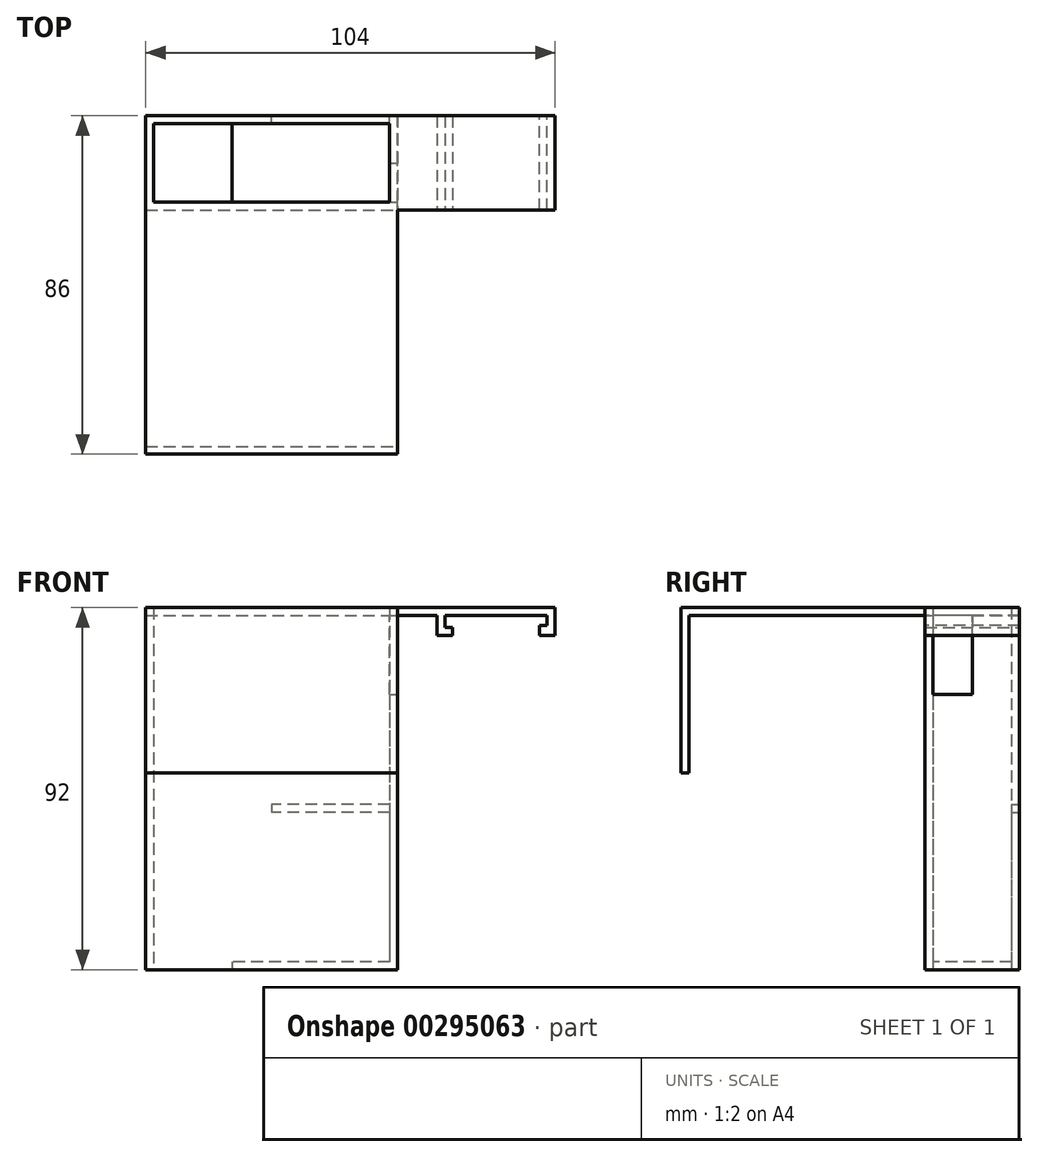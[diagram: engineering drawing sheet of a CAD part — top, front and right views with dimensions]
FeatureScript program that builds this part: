
annotation { "Feature Type Name" : "Feature", "Feature Type Description" : "" }
export const myFeature = defineFeature(function(context is Context, id is Id, definition is map)
    precondition{}
    {
        {
            var Q0;
            Q0=qCreatedBy(makeId("Top.planeOp"),FACE);
            var sketch = newSketch(context, id + "F0", { "sketchPlane" : qUnion([Q0])});
            skLineSegment(sketch, "E0.bottom", {"start": v(32, 32) * mm, "end": v(-32, 32) * mm});
            skLineSegment(sketch, "E0.top", {"start": v(32, -32) * mm, "end": v(-32, -32) * mm});
            skLineSegment(sketch, "E0.left", {"start": v(32, 32) * mm, "end": v(32, -32) * mm});
            skLineSegment(sketch, "E0.right", {"start": v(-32, 32) * mm, "end": v(-32, -32) * mm});
            skPoint(sketch, "E0.middle", {"position": v(0, 0) * mm});
            skSolve(sketch);
        }
        {
            var Q0;
            Q0=makeQuery(id+"F0.imprint","IMPRINT",FACE,{"disambiguationData":[TD([[makeQuery(id+"F0.imprint","IMPRINT",EDGE,{"derivedFrom":sQuery(id+"F0.wireOp",EDGE,"E0.bottom")}),1.0]])]});
            extrude(context, id + "F1", {"entities" : qUnion([Q0]), "depth" : 2 * mm});
        }
        {
            var Q0;
            Q0=makeQuery(id+"F1.opExtrude","CAP_FACE",FACE,{"disambiguationData":[OSD([sQuery(id+"F0.wireOp",EDGE,"E0.bottom"),sQuery(id+"F0.wireOp",EDGE,"E0.top"),sQuery(id+"F0.wireOp",EDGE,"E0.left"),sQuery(id+"F0.wireOp",EDGE,"E0.right")])],"isStart":true});
            var sketch = newSketch(context, id + "F2", { "sketchPlane" : qUnion([Q0])});
            skLineSegment(sketch, "E1.bottom", {"start": v(-32, 32) * mm, "end": v(32, 32) * mm});
            skLineSegment(sketch, "E1.top", {"start": v(-32, 30) * mm, "end": v(32, 30) * mm});
            skLineSegment(sketch, "E1.left", {"start": v(-32, 32) * mm, "end": v(-32, 30) * mm});
            skLineSegment(sketch, "E1.right", {"start": v(32, 32) * mm, "end": v(32, 30) * mm});
            skLineSegment(sketch, "E2.bottom", {"start": v(-32, -32) * mm, "end": v(32, -32) * mm});
            skLineSegment(sketch, "E2.top", {"start": v(-32, -30) * mm, "end": v(32, -30) * mm});
            skLineSegment(sketch, "E2.left", {"start": v(-32, -32) * mm, "end": v(-32, -30) * mm});
            skLineSegment(sketch, "E2.right", {"start": v(32, -32) * mm, "end": v(32, -30) * mm});
            skSolve(sketch);
        }
        {
            var Q0;
            Q0=makeQuery(id+"F2.imprint","IMPRINT",FACE,{"disambiguationData":[TD([[makeQuery(id+"F2.imprint","IMPRINT",EDGE,{"derivedFrom":sQuery(id+"F2.wireOp",EDGE,"E1.bottom")}),1.0]])]});
            extrude(context, id + "F3", {"entities" : qUnion([Q0]), "operationType" : NewBodyOperationType.ADD, "depth" : 25 * mm});
        }
        {
            var Q0;
            Q0=makeQuery(id+"F1.opExtrude","CAP_FACE",FACE,{"disambiguationData":[OSD([sQuery(id+"F0.wireOp",EDGE,"E0.bottom"),sQuery(id+"F0.wireOp",EDGE,"E0.top"),sQuery(id+"F0.wireOp",EDGE,"E0.left"),sQuery(id+"F0.wireOp",EDGE,"E0.right")])],"isStart":true});
            var sketch = newSketch(context, id + "F4", { "sketchPlane" : qUnion([Q0])});
            skLineSegment(sketch, "E3.bottom", {"start": v(-32, -32) * mm, "end": v(32, -32) * mm});
            skLineSegment(sketch, "E3.top", {"start": v(-32, -30) * mm, "end": v(32, -30) * mm});
            skLineSegment(sketch, "E3.left", {"start": v(-32, -32) * mm, "end": v(-32, -30) * mm});
            skLineSegment(sketch, "E3.right", {"start": v(32, -32) * mm, "end": v(32, -30) * mm});
            skSolve(sketch);
        }
        {
            var Q0;
            Q0=makeQuery(id+"F4.imprint","IMPRINT",FACE,{"disambiguationData":[TD([[makeQuery(id+"F4.imprint","IMPRINT",EDGE,{"derivedFrom":sQuery(id+"F4.wireOp",EDGE,"E3.bottom")}),-1.0]])]});
            extrude(context, id + "F5", {"entities" : qUnion([Q0]), "operationType" : NewBodyOperationType.ADD, "depth" : 90 * mm});
        }
        {
            var Q0;
            Q0=makeQuery(id+"F5.boolean.opBoolean","MERGE",FACE,{"derivedFrom":[makeQuery(id+"F1.opExtrude","SWEPT_FACE",FACE,{"disambiguationData":[OSD([sQuery(id+"F0.wireOp",EDGE,"E0.bottom")])]}),makeQuery(id+"F5.opExtrude","SWEPT_FACE",FACE,{"disambiguationData":[OSD([sQuery(id+"F4.wireOp",EDGE,"E3.bottom")])]})]});
            var sketch = newSketch(context, id + "F6", { "sketchPlane" : qUnion([Q0])});
            skLineSegment(sketch, "E4.bottom", {"start": v(-32, 2) * mm, "end": v(-30, 2) * mm});
            skLineSegment(sketch, "E4.top", {"start": v(-32, -90) * mm, "end": v(-30, -90) * mm});
            skLineSegment(sketch, "E4.left", {"start": v(-32, 2) * mm, "end": v(-32, -90) * mm});
            skLineSegment(sketch, "E4.right", {"start": v(-30, 2) * mm, "end": v(-30, -90) * mm});
            skSolve(sketch);
        }
        {
            var Q0;
            Q0=makeQuery(id+"F6.imprint","IMPRINT",FACE,{"disambiguationData":[TD([[makeQuery(id+"F6.imprint","IMPRINT",EDGE,{"derivedFrom":sQuery(id+"F6.wireOp",EDGE,"E4.bottom")}),-1.0]])]});
            extrude(context, id + "F7", {"entities" : qUnion([Q0]), "operationType" : NewBodyOperationType.ADD, "depth" : 22 * mm});
        }
        {
            var Q0;
            Q0=makeQuery(id+"F5.boolean.opBoolean","MERGE",FACE,{"derivedFrom":[makeQuery(id+"F1.opExtrude","SWEPT_FACE",FACE,{"disambiguationData":[OSD([sQuery(id+"F0.wireOp",EDGE,"E0.bottom")])]}),makeQuery(id+"F5.opExtrude","SWEPT_FACE",FACE,{"disambiguationData":[OSD([sQuery(id+"F4.wireOp",EDGE,"E3.bottom")])]})]});
            var sketch = newSketch(context, id + "F8", { "sketchPlane" : qUnion([Q0])});
            skLineSegment(sketch, "E5.bottom", {"start": v(32, 2) * mm, "end": v(30, 2) * mm});
            skLineSegment(sketch, "E5.top", {"start": v(32, -90) * mm, "end": v(30, -90) * mm});
            skLineSegment(sketch, "E5.left", {"start": v(32, 2) * mm, "end": v(32, -90) * mm});
            skLineSegment(sketch, "E5.right", {"start": v(30, 2) * mm, "end": v(30, -90) * mm});
            skSolve(sketch);
        }
        {
            var Q0;
            Q0=makeQuery(id+"F8.imprint","IMPRINT",FACE,{"disambiguationData":[TD([[makeQuery(id+"F8.imprint","IMPRINT",EDGE,{"derivedFrom":sQuery(id+"F8.wireOp",EDGE,"E5.bottom")}),-1.0]])]});
            extrude(context, id + "F9", {"entities" : qUnion([Q0]), "operationType" : NewBodyOperationType.ADD, "depth" : 22 * mm});
        }
        {
            var Q0;
            Q0=makeQuery(id+"F7.opExtrude","SWEPT_FACE",FACE,{"disambiguationData":[OSD([sQuery(id+"F6.wireOp",EDGE,"E4.right")])]});
            var sketch = newSketch(context, id + "F10", { "sketchPlane" : qUnion([Q0])});
            skLineSegment(sketch, "E6.bottom", {"start": v(-54, 2) * mm, "end": v(-52, 2) * mm});
            skLineSegment(sketch, "E6.top", {"start": v(-54, -90) * mm, "end": v(-52, -90) * mm});
            skLineSegment(sketch, "E6.left", {"start": v(-54, 2) * mm, "end": v(-54, -90) * mm});
            skLineSegment(sketch, "E6.right", {"start": v(-52, 2) * mm, "end": v(-52, -90) * mm});
            skSolve(sketch);
        }
        {
            var Q0;
            Q0=makeQuery(id+"F10.imprint","IMPRINT",FACE,{"disambiguationData":[TD([[makeQuery(id+"F10.imprint","IMPRINT",EDGE,{"derivedFrom":sQuery(id+"F10.wireOp",EDGE,"E6.bottom")}),-1.0]])]});
            extrude(context, id + "F11", {"entities" : qUnion([Q0]), "operationType" : NewBodyOperationType.ADD, "depth" : 60 * mm});
        }
        {
            var Q0;
            Q0=makeQuery(id+"F5.boolean.opBoolean","MERGE",FACE,{"derivedFrom":[makeQuery(id+"F1.opExtrude","SWEPT_FACE",FACE,{"disambiguationData":[OSD([sQuery(id+"F0.wireOp",EDGE,"E0.bottom")])]}),makeQuery(id+"F5.opExtrude","SWEPT_FACE",FACE,{"disambiguationData":[OSD([sQuery(id+"F4.wireOp",EDGE,"E3.bottom")])]})]});
            var sketch = newSketch(context, id + "F12", { "sketchPlane" : qUnion([Q0])});
            skLineSegment(sketch, "E7.bottom", {"start": v(-30, -90) * mm, "end": v(30, -90) * mm});
            skLineSegment(sketch, "E7.top", {"start": v(-30, -88) * mm, "end": v(30, -88) * mm});
            skLineSegment(sketch, "E7.left", {"start": v(-30, -90) * mm, "end": v(-30, -88) * mm});
            skLineSegment(sketch, "E7.right", {"start": v(30, -90) * mm, "end": v(30, -88) * mm});
            skSolve(sketch);
        }
        {
            var Q0;
            Q0=makeQuery(id+"F12.imprint","IMPRINT",FACE,{"disambiguationData":[TD([[makeQuery(id+"F12.imprint","IMPRINT",EDGE,{"derivedFrom":sQuery(id+"F12.wireOp",EDGE,"E7.bottom")}),1.0]])]});
            extrude(context, id + "F13", {"entities" : qUnion([Q0]), "operationType" : NewBodyOperationType.ADD, "depth" : 20 * mm});
        }
        {
            var Q0;
            Q0=makeQuery(id+"F7.boolean.opBoolean","MERGE",FACE,{"derivedFrom":[makeQuery(id+"F5.boolean.opBoolean","MERGE",FACE,{"derivedFrom":[makeQuery(id+"F3.boolean.opBoolean","MERGE",FACE,{"derivedFrom":[makeQuery(id+"F1.opExtrude","SWEPT_FACE",FACE,{"disambiguationData":[OSD([sQuery(id+"F0.wireOp",EDGE,"E0.left")])]}),makeQuery(id+"F3.opExtrude","SWEPT_FACE",FACE,{"disambiguationData":[OSD([sQuery(id+"F2.wireOp",EDGE,"E1.right")])]})]}),makeQuery(id+"F5.opExtrude","SWEPT_FACE",FACE,{"disambiguationData":[OSD([sQuery(id+"F4.wireOp",EDGE,"E3.right")])]})]}),makeQuery(id+"F7.opExtrude","SWEPT_FACE",FACE,{"disambiguationData":[OSD([sQuery(id+"F6.wireOp",EDGE,"E4.left")])]})]});
            var sketch = newSketch(context, id + "F14", { "sketchPlane" : qUnion([Q0])});
            skLineSegment(sketch, "E8.bottom", {"start": v(32, 0) * mm, "end": v(42, 0) * mm});
            skLineSegment(sketch, "E8.top", {"start": v(32, -20) * mm, "end": v(42, -20) * mm});
            skLineSegment(sketch, "E8.left", {"start": v(32, 0) * mm, "end": v(32, -20) * mm});
            skLineSegment(sketch, "E8.right", {"start": v(42, 0) * mm, "end": v(42, -20) * mm});
            skSolve(sketch);
        }
        {
            var Q0;
            Q0=makeQuery(id+"F14.imprint","IMPRINT",FACE,{"disambiguationData":[TD([[makeQuery(id+"F14.imprint","IMPRINT",EDGE,{"derivedFrom":sQuery(id+"F14.wireOp",EDGE,"E8.bottom")}),-1.0]])]});
            extrude(context, id + "F15", {"entities" : qUnion([Q0]), "operationType" : NewBodyOperationType.REMOVE, "oppositeDirection" : true, "depth" : 25 * mm});
        }
        {
            var Q0;
            Q0=makeQuery(id+"F13.boolean.opBoolean","MERGE",FACE,{"derivedFrom":[makeQuery(id+"F11.boolean.opBoolean","MERGE",FACE,{"derivedFrom":[makeQuery(id+"F9.boolean.opBoolean","MERGE",FACE,{"derivedFrom":[makeQuery(id+"F7.boolean.opBoolean","MERGE",FACE,{"derivedFrom":[makeQuery(id+"F5.opExtrude","CAP_FACE",FACE,{"disambiguationData":[OSD([sQuery(id+"F4.wireOp",EDGE,"E3.bottom"),sQuery(id+"F4.wireOp",EDGE,"E3.top"),sQuery(id+"F4.wireOp",EDGE,"E3.left"),sQuery(id+"F4.wireOp",EDGE,"E3.right")])],"isStart":false}),makeQuery(id+"F7.opExtrude","SWEPT_FACE",FACE,{"disambiguationData":[OSD([sQuery(id+"F6.wireOp",EDGE,"E4.top")])]})]}),makeQuery(id+"F9.opExtrude","SWEPT_FACE",FACE,{"disambiguationData":[OSD([sQuery(id+"F8.wireOp",EDGE,"E5.top")])]})]}),makeQuery(id+"F11.opExtrude","SWEPT_FACE",FACE,{"disambiguationData":[OSD([sQuery(id+"F10.wireOp",EDGE,"E6.top")])]})]}),makeQuery(id+"F13.opExtrude","SWEPT_FACE",FACE,{"disambiguationData":[OSD([sQuery(id+"F12.wireOp",EDGE,"E7.bottom")])]})]});
            var sketch = newSketch(context, id + "F16", { "sketchPlane" : qUnion([Q0])});
            skLineSegment(sketch, "E9.bottom", {"start": v(-30, -32) * mm, "end": v(-10, -32) * mm});
            skLineSegment(sketch, "E9.top", {"start": v(-30, -52) * mm, "end": v(-10, -52) * mm});
            skLineSegment(sketch, "E9.left", {"start": v(-30, -32) * mm, "end": v(-30, -52) * mm});
            skLineSegment(sketch, "E9.right", {"start": v(-10, -32) * mm, "end": v(-10, -52) * mm});
            skSolve(sketch);
        }
        {
            var Q0;
            Q0=makeQuery(id+"F16.imprint","IMPRINT",FACE,{"disambiguationData":[TD([[makeQuery(id+"F16.imprint","IMPRINT",EDGE,{"derivedFrom":sQuery(id+"F16.wireOp",EDGE,"E9.bottom")}),-1.0]])]});
            extrude(context, id + "F17", {"entities" : qUnion([Q0]), "operationType" : NewBodyOperationType.REMOVE, "oppositeDirection" : true, "depth" : 25 * mm});
        }
        {
            var Q0;
            Q0=makeQuery(id+"F3.opExtrude","CAP_FACE",FACE,{"disambiguationData":[OSD([sQuery(id+"F2.wireOp",EDGE,"E1.bottom"),sQuery(id+"F2.wireOp",EDGE,"E1.top"),sQuery(id+"F2.wireOp",EDGE,"E1.left"),sQuery(id+"F2.wireOp",EDGE,"E1.right")])],"isStart":false});
            extrude(context, id + "F18", {"entities" : qUnion([Q0]), "operationType" : NewBodyOperationType.ADD, "depth" : 15 * mm});
        }
        {
            var Q0;
            Q0=makeQuery(id+"F11.boolean.opBoolean","MERGE",FACE,{"derivedFrom":[makeQuery(id+"F7.opExtrude","CAP_FACE",FACE,{"disambiguationData":[OSD([sQuery(id+"F6.wireOp",EDGE,"E4.bottom"),sQuery(id+"F6.wireOp",EDGE,"E4.top"),sQuery(id+"F6.wireOp",EDGE,"E4.left"),sQuery(id+"F6.wireOp",EDGE,"E4.right")])],"isStart":false}),makeQuery(id+"F9.opExtrude","CAP_FACE",FACE,{"disambiguationData":[OSD([sQuery(id+"F8.wireOp",EDGE,"E5.bottom"),sQuery(id+"F8.wireOp",EDGE,"E5.top"),sQuery(id+"F8.wireOp",EDGE,"E5.left"),sQuery(id+"F8.wireOp",EDGE,"E5.right")])],"isStart":false}),makeQuery(id+"F11.opExtrude","SWEPT_FACE",FACE,{"disambiguationData":[OSD([sQuery(id+"F10.wireOp",EDGE,"E6.left")])]})]});
            var sketch = newSketch(context, id + "F19", { "sketchPlane" : qUnion([Q0])});
            skLineSegment(sketch, "E10.bottom", {"start": v(-30, -48) * mm, "end": v(0, -48) * mm});
            skLineSegment(sketch, "E10.top", {"start": v(-30, -50) * mm, "end": v(0, -50) * mm});
            skLineSegment(sketch, "E10.left", {"start": v(-30, -48) * mm, "end": v(-30, -50) * mm});
            skLineSegment(sketch, "E10.right", {"start": v(0, -48) * mm, "end": v(0, -50) * mm});
            skSolve(sketch);
        }
        {
            var Q0;
            Q0=makeQuery(id+"F19.imprint","IMPRINT",FACE,{"disambiguationData":[TD([[makeQuery(id+"F19.imprint","IMPRINT",EDGE,{"derivedFrom":sQuery(id+"F19.wireOp",EDGE,"E10.bottom")}),-1.0]])]});
            extrude(context, id + "F20", {"entities" : qUnion([Q0]), "operationType" : NewBodyOperationType.REMOVE, "oppositeDirection" : true, "depth" : 2 * mm});
        }
        {
            var Q0;
            {var subQ0=sQuery(id+"F2.wireOp",EDGE,"E1.right");Q0=makeQuery(id+"F18.boolean.opBoolean","MERGE",FACE,{"derivedFrom":[makeQuery(id+"F7.boolean.opBoolean","MERGE",FACE,{"derivedFrom":[makeQuery(id+"F5.boolean.opBoolean","MERGE",FACE,{"derivedFrom":[makeQuery(id+"F3.boolean.opBoolean","MERGE",FACE,{"derivedFrom":[makeQuery(id+"F1.opExtrude","SWEPT_FACE",FACE,{"disambiguationData":[OSD([sQuery(id+"F0.wireOp",EDGE,"E0.left")])]}),makeQuery(id+"F3.opExtrude","SWEPT_FACE",FACE,{"disambiguationData":[OSD([subQ0])]})]}),makeQuery(id+"F5.opExtrude","SWEPT_FACE",FACE,{"disambiguationData":[OSD([sQuery(id+"F4.wireOp",EDGE,"E3.right")])]})]}),makeQuery(id+"F7.opExtrude","SWEPT_FACE",FACE,{"disambiguationData":[OSD([sQuery(id+"F6.wireOp",EDGE,"E4.left")])]})]}),makeQuery(id+"F18.opExtrude","SWEPT_FACE",FACE,{"disambiguationData":[OSD([subQ0])]})]});}
            var sketch = newSketch(context, id + "F21", { "sketchPlane" : qUnion([Q0])});
            skLineSegment(sketch, "E11.bottom", {"start": v(30, 0) * mm, "end": v(54, 0) * mm});
            skLineSegment(sketch, "E11.top", {"start": v(30, 2) * mm, "end": v(54, 2) * mm});
            skLineSegment(sketch, "E11.left", {"start": v(30, 0) * mm, "end": v(30, 2) * mm});
            skLineSegment(sketch, "E11.right", {"start": v(54, 0) * mm, "end": v(54, 2) * mm});
            skSolve(sketch);
        }
        {
            var Q0;
            Q0=makeQuery(id+"F21.imprint","IMPRINT",FACE,{"disambiguationData":[TD([[makeQuery(id+"F21.imprint","IMPRINT",EDGE,{"derivedFrom":sQuery(id+"F21.wireOp",EDGE,"E11.top")}),1.0]])]});
            extrude(context, id + "F22", {"entities" : qUnion([Q0]), "operationType" : NewBodyOperationType.ADD, "depth" : 40 * mm});
        }
        {
            var Q0;
            Q0=makeQuery(id+"F22.boolean.opBoolean","MERGE",FACE,{"derivedFrom":[makeQuery(id+"F15.boolean.opBoolean","COPY",FACE,{"derivedFrom":makeQuery(id+"F15.opExtrude","SWEPT_FACE",FACE,{"disambiguationData":[OSD([sQuery(id+"F14.wireOp",EDGE,"E8.bottom")])]})}),makeQuery(id+"F22.opExtrude","SWEPT_FACE",FACE,{"disambiguationData":[OSD([sQuery(id+"F21.wireOp",EDGE,"E11.bottom")])]})]});
            var sketch = newSketch(context, id + "F23", { "sketchPlane" : qUnion([Q0])});
            skLineSegment(sketch, "E12.bottom", {"start": v(72, -30) * mm, "end": v(70, -30) * mm});
            skLineSegment(sketch, "E12.top", {"start": v(72, -54) * mm, "end": v(70, -54) * mm});
            skLineSegment(sketch, "E12.left", {"start": v(72, -30) * mm, "end": v(72, -54) * mm});
            skLineSegment(sketch, "E12.right", {"start": v(70, -30) * mm, "end": v(70, -54) * mm});
            skLineSegment(sketch, "E13.right", {"start": v(44, -54) * mm, "end": v(44, -47.91) * mm});
            skLineSegment(sketch, "E14.bottom", {"start": v(44, -54) * mm, "end": v(42, -54) * mm});
            skLineSegment(sketch, "E14.top", {"start": v(44, -30) * mm, "end": v(42, -30) * mm});
            skLineSegment(sketch, "E14.left", {"start": v(44, -54) * mm, "end": v(44, -30) * mm});
            skLineSegment(sketch, "E14.right", {"start": v(42, -54) * mm, "end": v(42, -30) * mm});
            skSolve(sketch);
        }
        {
            var Q0;
            Q0=makeQuery(id+"F23.imprint","IMPRINT",FACE,{"disambiguationData":[TD([[makeQuery(id+"F23.imprint","IMPRINT",EDGE,{"derivedFrom":sQuery(id+"F23.wireOp",EDGE,"E12.bottom")}),1.0]])]});
            var Q1;
            {var subQ4=sQuery(id+"F23.wireOp",EDGE,"E14.bottom");Q1=makeQuery(id+"F23.imprint","IMPRINT",FACE,{"disambiguationData":[TD([[makeQuery(id+"F23.imprint","IMPRINT",EDGE,{"derivedFrom":subQ4}),-1.0]])]});}
            extrude(context, id + "F24", {"entities" : qUnion([Q0, Q1]), "operationType" : NewBodyOperationType.ADD, "depth" : 5 * mm});
        }
        {
            var Q0;
            Q0=makeQuery(id+"F24.opExtrude","SWEPT_FACE",FACE,{"disambiguationData":[OSD([sQuery(id+"F23.wireOp",EDGE,"E14.left")])]});
            var sketch = newSketch(context, id + "F25", { "sketchPlane" : qUnion([Q0])});
            skLineSegment(sketch, "E15.bottom", {"start": v(30, -5) * mm, "end": v(54, -5) * mm});
            skLineSegment(sketch, "E15.top", {"start": v(30, -3) * mm, "end": v(54, -3) * mm});
            skLineSegment(sketch, "E15.left", {"start": v(30, -5) * mm, "end": v(30, -3) * mm});
            skLineSegment(sketch, "E15.right", {"start": v(54, -5) * mm, "end": v(54, -3) * mm});
            skSolve(sketch);
        }
        {
            var Q0;
            Q0=makeQuery(id+"F25.imprint","IMPRINT",FACE,{"disambiguationData":[TD([[makeQuery(id+"F25.imprint","IMPRINT",EDGE,{"derivedFrom":sQuery(id+"F25.wireOp",EDGE,"E15.bottom")}),-1.0]])]});
            extrude(context, id + "F26", {"entities" : qUnion([Q0]), "operationType" : NewBodyOperationType.ADD, "depth" : 2 * mm});
        }
        {
            var Q0;
            Q0=makeQuery(id+"F24.opExtrude","SWEPT_FACE",FACE,{"disambiguationData":[OSD([sQuery(id+"F23.wireOp",EDGE,"E12.right")])]});
            var sketch = newSketch(context, id + "F27", { "sketchPlane" : qUnion([Q0])});
            skLineSegment(sketch, "E16.bottom", {"start": v(-54, -5) * mm, "end": v(-30, -5) * mm});
            skLineSegment(sketch, "E16.top", {"start": v(-54, -2.5) * mm, "end": v(-30, -2.5) * mm});
            skLineSegment(sketch, "E16.left", {"start": v(-54, -5) * mm, "end": v(-54, -2.5) * mm});
            skLineSegment(sketch, "E16.right", {"start": v(-30, -5) * mm, "end": v(-30, -2.5) * mm});
            skSolve(sketch);
        }
        {
            var Q0;
            Q0=makeQuery(id+"F27.imprint","IMPRINT",FACE,{"disambiguationData":[TD([[makeQuery(id+"F27.imprint","IMPRINT",EDGE,{"derivedFrom":sQuery(id+"F27.wireOp",EDGE,"E16.bottom")}),-1.0]])]});
            extrude(context, id + "F28", {"entities" : qUnion([Q0]), "operationType" : NewBodyOperationType.ADD, "depth" : 2 * mm});
        }
    });
